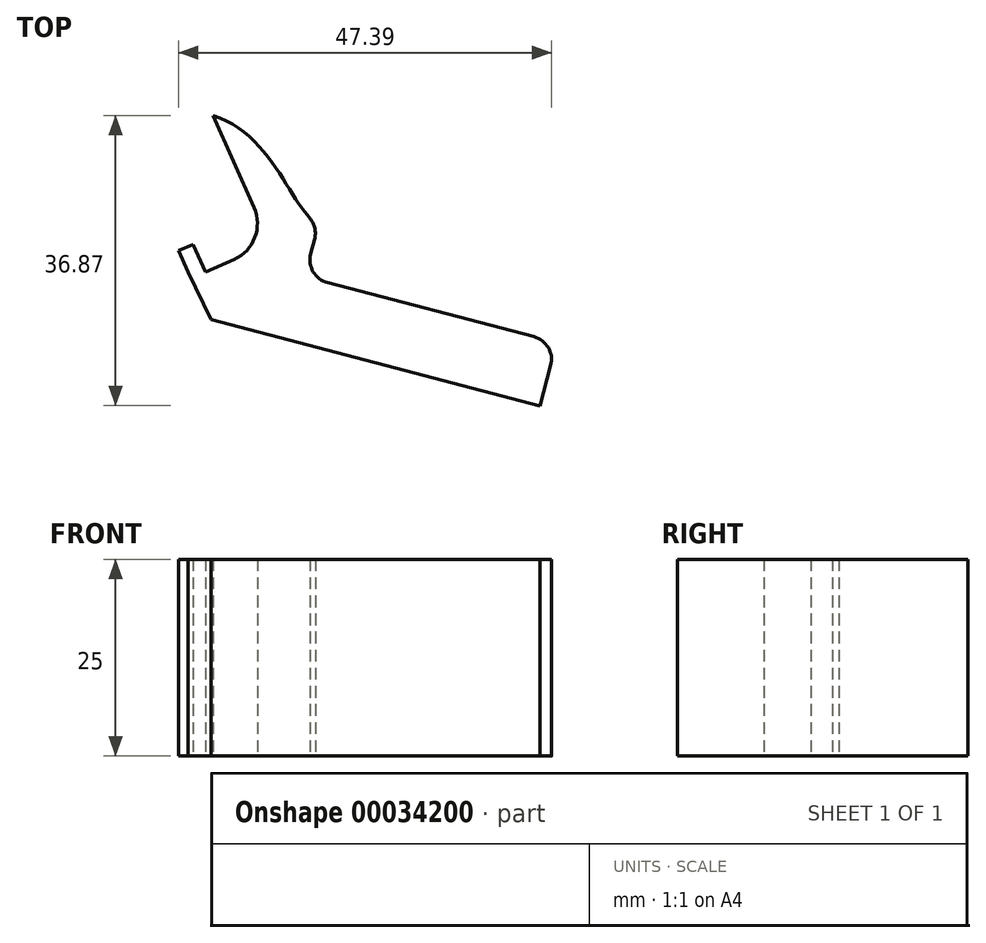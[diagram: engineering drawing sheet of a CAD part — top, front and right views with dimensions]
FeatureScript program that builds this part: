
annotation { "Feature Type Name" : "Feature", "Feature Type Description" : "" }
export const myFeature = defineFeature(function(context is Context, id is Id, definition is map)
    precondition{}
    {
        {
            var Q0;
            Q0=qCreatedBy(makeId("Top.planeOp"),FACE);
            var sketch = newSketch(context, id + "F0", { "sketchPlane" : qUnion([Q0])});
            skLineSegment(sketch, "E0", {"start": v(-52.63, -70.73) * mm, "end": v(-52.63, -64.73) * mm, "construction": true});
            skLineSegment(sketch, "E1", {"start": v(-51.8, -64.73) * mm, "end": v(-48.9, -70.73) * mm});
            skLineSegment(sketch, "E2", {"start": v(-51.8, -64.73) * mm, "end": v(-53.02, -61.99) * mm});
            skLineSegment(sketch, "E3", {"start": v(-53.02, -61.99) * mm, "end": v(-51.2, -61.17) * mm});
            skLineSegment(sketch, "E4", {"start": v(-51.2, -61.17) * mm, "end": v(-49.6, -64.73) * mm});
            skLineSegment(sketch, "E5", {"start": v(-49.6, -64.73) * mm, "end": v(-45.96, -63.1) * mm});
            skLineSegment(sketch, "E6", {"start": v(-43.42, -56.5) * mm, "end": v(-48.64, -44.8) * mm});
            skFitSpline(sketch, "E7", {"points": [v(-48.64, -44.8) * mm, v(-37.73, -56) * mm, v(-34.2, -61.06) * mm], "startDerivative": vector(28.22, -8.51) * mm, "endDerivative": vector(4.8, -12.87) * mm});
            skPoint(sketch, "E8.visualSharp", {"position": v(-41.39, -61.06) * mm});
            skArc(sketch, "E8.filletArc", {"start": v(-45.96, -63.1) * mm, "mid": v(-43.32, -60.32) * mm, "end": v(-43.42, -56.5) * mm});
            skPoint(sketch, "E9.end.orphan", {"position": v(-5.43, -70.73) * mm});
            skLineSegment(sketch, "E10", {"start": v(-48.9, -70.73) * mm, "end": v(-7.07, -81.68) * mm});
            skLineSegment(sketch, "E11", {"start": v(-7.07, -81.68) * mm, "end": v(-5.73, -76.58) * mm});
            skLineSegment(sketch, "E12", {"start": v(-7.87, -72.92) * mm, "end": v(-34.07, -66.06) * mm});
            skLineSegment(sketch, "E13", {"start": v(-36.22, -62.4) * mm, "end": v(-35.73, -60.54) * mm});
            skPoint(sketch, "E14.visualSharp", {"position": v(-35.35, -59.1) * mm});
            skArc(sketch, "E14.filletArc", {"start": v(-35.73, -60.54) * mm, "mid": v(-35.7, -59.15) * mm, "end": v(-36.3, -57.9) * mm});
            skPoint(sketch, "E15.visualSharp", {"position": v(-36.97, -65.3) * mm});
            skArc(sketch, "E15.filletArc", {"start": v(-36.22, -62.4) * mm, "mid": v(-35.9, -64.67) * mm, "end": v(-34.07, -66.06) * mm});
            skPoint(sketch, "E16.visualSharp", {"position": v(-4.97, -73.68) * mm});
            skArc(sketch, "E16.filletArc", {"start": v(-5.73, -76.58) * mm, "mid": v(-6.04, -74.3) * mm, "end": v(-7.87, -72.92) * mm});
            skSolve(sketch);
        }
        {
            var Q0;
            Q0=makeQuery(id+"F0.imprint","IMPRINT",FACE,{"disambiguationData":[TD([[makeQuery(id+"F0.imprint","IMPRINT",EDGE,{"derivedFrom":sQuery(id+"F0.wireOp",EDGE,"E1")}),1.0]])]});
            extrude(context, id + "F1", {"entities" : qUnion([Q0]), "depth" : 25 * mm});
        }
    });
